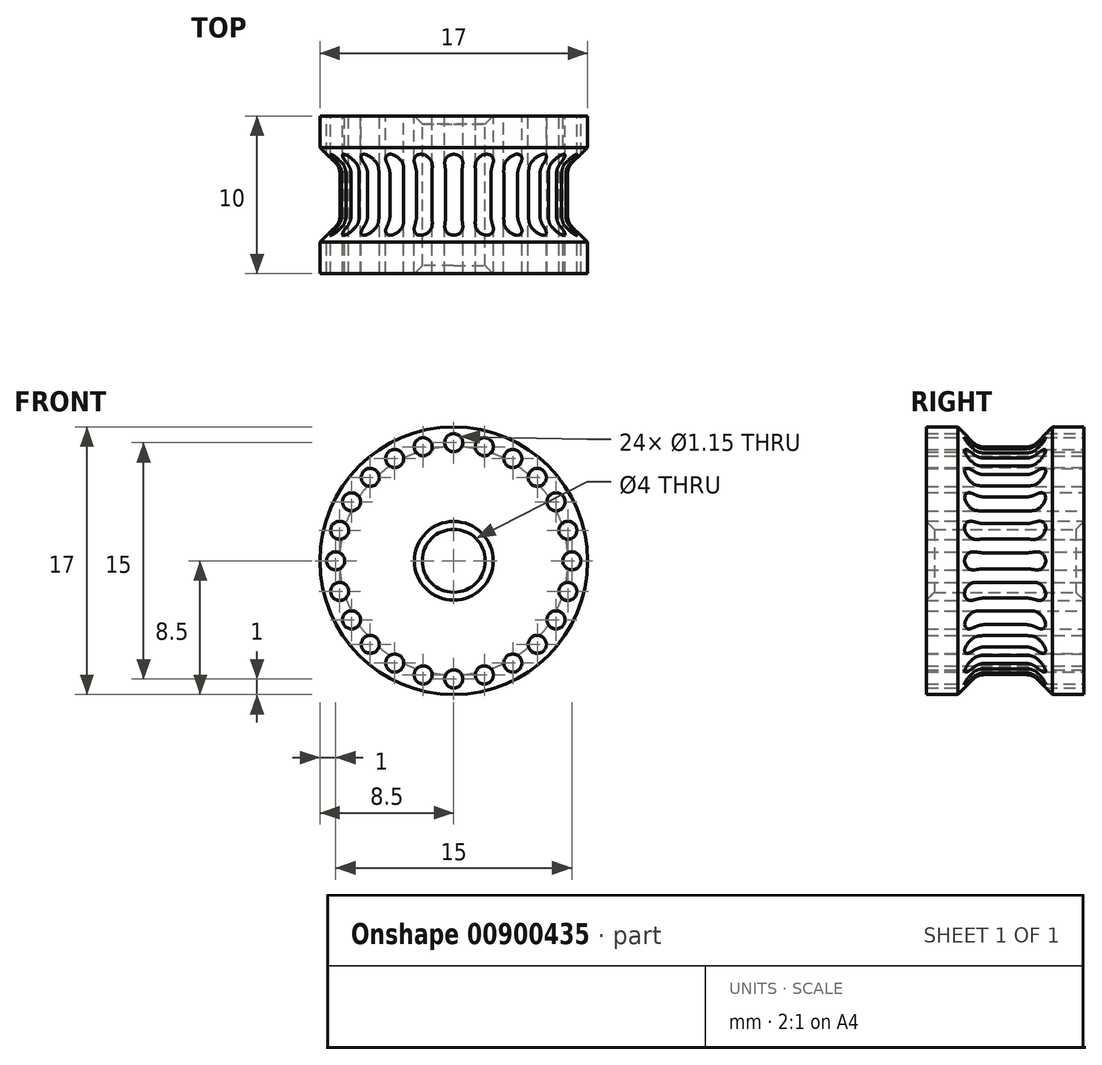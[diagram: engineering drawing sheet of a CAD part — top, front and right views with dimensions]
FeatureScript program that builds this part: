
annotation { "Feature Type Name" : "Feature", "Feature Type Description" : "" }
export const myFeature = defineFeature(function(context is Context, id is Id, definition is map)
    precondition{}
    {
        {
            var Q0;
            Q0=qCreatedBy(makeId("Right.planeOp"),FACE);
            var sketch = newSketch(context, id + "F0", { "sketchPlane" : qUnion([Q0])});
            skLineSegment(sketch, "E0", {"start": v(0, 2) * mm, "end": v(0, 8.5) * mm});
            skLineSegment(sketch, "E1", {"start": v(0, 8.5) * mm, "end": v(-2, 8.5) * mm});
            skLineSegment(sketch, "E2", {"start": v(-2, 8.5) * mm, "end": v(-2.96, 7.54) * mm});
            skLineSegment(sketch, "E3", {"start": v(-3.66, 7.25) * mm, "end": v(-6.34, 7.25) * mm});
            skLineSegment(sketch, "E4", {"start": v(-7.04, 7.54) * mm, "end": v(-8, 8.5) * mm});
            skLineSegment(sketch, "E5", {"start": v(-8, 8.5) * mm, "end": v(-10, 8.5) * mm});
            skLineSegment(sketch, "E6", {"start": v(-10, 8.5) * mm, "end": v(-10, 2) * mm});
            skLineSegment(sketch, "E7", {"start": v(-10, 2) * mm, "end": v(0, 2) * mm});
            skLineSegment(sketch, "E8", {"start": v(-10, 7.5) * mm, "end": v(0, 7.5) * mm, "construction": true});
            skLineSegment(sketch, "E9", {"start": v(-7, 8.5) * mm, "end": v(-7, 7.5) * mm, "construction": true});
            skLineSegment(sketch, "E10", {"start": v(-3, 8.5) * mm, "end": v(-3, 7.5) * mm, "construction": true});
            skLineSegment(sketch, "E11", {"start": v(0, 0) * mm, "end": v(-10, 0) * mm, "construction": true});
            skPoint(sketch, "E12.visualSharp", {"position": v(-6.75, 7.25) * mm});
            skArc(sketch, "E12.filletArc", {"start": v(-7.04, 7.54) * mm, "mid": v(-6.72, 7.33) * mm, "end": v(-6.34, 7.25) * mm});
            skPoint(sketch, "E13.visualSharp", {"position": v(-3.25, 7.25) * mm});
            skArc(sketch, "E13.filletArc", {"start": v(-3.66, 7.25) * mm, "mid": v(-3.28, 7.33) * mm, "end": v(-2.96, 7.54) * mm});
            skSolve(sketch);
        }
        {
            var Q0;
            Q0=makeQuery(id+"F0.imprint","IMPRINT",FACE,{"disambiguationData":[TD([[makeQuery(id+"F0.imprint","IMPRINT",EDGE,{"derivedFrom":sQuery(id+"F0.wireOp",EDGE,"E0")}),1.0]])]});
            var Q1;
            Q1=sQuery(id+"F0.wireOp",EDGE,"E11");
            revolve(context, id + "F1", {"surfaceOperationType" : NewSurfaceOperationType.NEW, "entities" : qUnion([Q0]), "axis" : qUnion([Q1]), "revolveType" : RevolveType.FULL});
        }
        {
            var Q0;
            Q0=qCreatedBy(makeId("Front.planeOp"),FACE);
            var sketch = newSketch(context, id + "F2", { "sketchPlane" : qUnion([Q0])});
            skCircle(sketch, "E14", {"center": v(0, 7.5) * mm, "radius": 0.57 * mm});
            skCircle(sketch, "E15.1.0", {"center": v(-1.94, 7.24) * mm, "radius": 0.57 * mm});
            skCircle(sketch, "E15.2.0", {"center": v(-3.75, 6.5) * mm, "radius": 0.57 * mm});
            skPoint(sketch, "E15.center", {"position": v(0, 0) * mm});
            skCircle(sketch, "E16.1.3.0", {"center": v(-5.3, 5.3) * mm, "radius": 0.57 * mm});
            skCircle(sketch, "E16.1.4.0", {"center": v(-6.5, 3.75) * mm, "radius": 0.57 * mm});
            skCircle(sketch, "E16.1.5.0", {"center": v(-7.24, 1.94) * mm, "radius": 0.57 * mm});
            skCircle(sketch, "E16.1.6.0", {"center": v(-7.5, 0) * mm, "radius": 0.57 * mm});
            skCircle(sketch, "E16.1.7.0", {"center": v(-7.24, -1.94) * mm, "radius": 0.57 * mm});
            skCircle(sketch, "E16.1.8.0", {"center": v(-6.5, -3.75) * mm, "radius": 0.57 * mm});
            skCircle(sketch, "E16.1.9.0", {"center": v(-5.3, -5.3) * mm, "radius": 0.57 * mm});
            skCircle(sketch, "E16.1.10.0", {"center": v(-3.75, -6.5) * mm, "radius": 0.57 * mm});
            skCircle(sketch, "E16.1.11.0", {"center": v(-1.94, -7.24) * mm, "radius": 0.57 * mm});
            skCircle(sketch, "E17.1.12.0", {"center": v(0, -7.5) * mm, "radius": 0.57 * mm});
            skCircle(sketch, "E17.1.13.0", {"center": v(1.94, -7.24) * mm, "radius": 0.57 * mm});
            skCircle(sketch, "E17.1.14.0", {"center": v(3.75, -6.5) * mm, "radius": 0.57 * mm});
            skCircle(sketch, "E17.1.15.0", {"center": v(5.3, -5.3) * mm, "radius": 0.57 * mm});
            skCircle(sketch, "E17.1.16.0", {"center": v(6.5, -3.75) * mm, "radius": 0.57 * mm});
            skCircle(sketch, "E17.1.17.0", {"center": v(7.24, -1.94) * mm, "radius": 0.57 * mm});
            skCircle(sketch, "E17.1.18.0", {"center": v(7.5, 0) * mm, "radius": 0.57 * mm});
            skCircle(sketch, "E17.1.19.0", {"center": v(7.24, 1.94) * mm, "radius": 0.57 * mm});
            skCircle(sketch, "E17.1.20.0", {"center": v(6.5, 3.75) * mm, "radius": 0.57 * mm});
            skCircle(sketch, "E17.1.21.0", {"center": v(5.3, 5.3) * mm, "radius": 0.57 * mm});
            skCircle(sketch, "E17.1.22.0", {"center": v(3.75, 6.5) * mm, "radius": 0.57 * mm});
            skCircle(sketch, "E17.1.23.0", {"center": v(1.94, 7.24) * mm, "radius": 0.57 * mm});
            skSolve(sketch);
        }
        {
            var Q0;
            Q0=makeQuery(id+"F2.imprint","IMPRINT",FACE,{"disambiguationData":[TD([[makeQuery(id+"F2.imprint","IMPRINT",EDGE,{"derivedFrom":sQuery(id+"F2.wireOp",EDGE,"E16.1.11.0")}),1.0]])]});
            var Q1;
            Q1=makeQuery(id+"F2.imprint","IMPRINT",FACE,{"disambiguationData":[TD([[makeQuery(id+"F2.imprint","IMPRINT",EDGE,{"derivedFrom":sQuery(id+"F2.wireOp",EDGE,"E17.1.14.0")}),1.0]])]});
            var Q2;
            Q2=makeQuery(id+"F2.imprint","IMPRINT",FACE,{"disambiguationData":[TD([[makeQuery(id+"F2.imprint","IMPRINT",EDGE,{"derivedFrom":sQuery(id+"F2.wireOp",EDGE,"E16.1.8.0")}),1.0]])]});
            var Q3;
            Q3=makeQuery(id+"F2.imprint","IMPRINT",FACE,{"disambiguationData":[TD([[makeQuery(id+"F2.imprint","IMPRINT",EDGE,{"derivedFrom":sQuery(id+"F2.wireOp",EDGE,"E15.2.0")}),1.0]])]});
            var Q4;
            Q4=makeQuery(id+"F2.imprint","IMPRINT",FACE,{"disambiguationData":[TD([[makeQuery(id+"F2.imprint","IMPRINT",EDGE,{"derivedFrom":sQuery(id+"F2.wireOp",EDGE,"E16.1.7.0")}),1.0]])]});
            var Q5;
            Q5=makeQuery(id+"F2.imprint","IMPRINT",FACE,{"disambiguationData":[TD([[makeQuery(id+"F2.imprint","IMPRINT",EDGE,{"derivedFrom":sQuery(id+"F2.wireOp",EDGE,"E16.1.4.0")}),1.0]])]});
            var Q6;
            Q6=makeQuery(id+"F2.imprint","IMPRINT",FACE,{"disambiguationData":[TD([[makeQuery(id+"F2.imprint","IMPRINT",EDGE,{"derivedFrom":sQuery(id+"F2.wireOp",EDGE,"E17.1.23.0")}),1.0]])]});
            var Q7;
            Q7=makeQuery(id+"F2.imprint","IMPRINT",FACE,{"disambiguationData":[TD([[makeQuery(id+"F2.imprint","IMPRINT",EDGE,{"derivedFrom":sQuery(id+"F2.wireOp",EDGE,"E17.1.15.0")}),1.0]])]});
            var Q8;
            Q8=makeQuery(id+"F2.imprint","IMPRINT",FACE,{"disambiguationData":[TD([[makeQuery(id+"F2.imprint","IMPRINT",EDGE,{"derivedFrom":sQuery(id+"F2.wireOp",EDGE,"E17.1.20.0")}),1.0]])]});
            var Q9;
            Q9=makeQuery(id+"F2.imprint","IMPRINT",FACE,{"disambiguationData":[TD([[makeQuery(id+"F2.imprint","IMPRINT",EDGE,{"derivedFrom":sQuery(id+"F2.wireOp",EDGE,"E15.1.0")}),1.0]])]});
            var Q10;
            Q10=makeQuery(id+"F2.imprint","IMPRINT",FACE,{"disambiguationData":[TD([[makeQuery(id+"F2.imprint","IMPRINT",EDGE,{"derivedFrom":sQuery(id+"F2.wireOp",EDGE,"E17.1.17.0")}),1.0]])]});
            var Q11;
            Q11=makeQuery(id+"F2.imprint","IMPRINT",FACE,{"disambiguationData":[TD([[makeQuery(id+"F2.imprint","IMPRINT",EDGE,{"derivedFrom":sQuery(id+"F2.wireOp",EDGE,"E16.1.6.0")}),1.0]])]});
            var Q12;
            Q12=makeQuery(id+"F2.imprint","IMPRINT",FACE,{"disambiguationData":[TD([[makeQuery(id+"F2.imprint","IMPRINT",EDGE,{"derivedFrom":sQuery(id+"F2.wireOp",EDGE,"E16.1.3.0")}),1.0]])]});
            var Q13;
            Q13=makeQuery(id+"F2.imprint","IMPRINT",FACE,{"disambiguationData":[TD([[makeQuery(id+"F2.imprint","IMPRINT",EDGE,{"derivedFrom":sQuery(id+"F2.wireOp",EDGE,"E17.1.22.0")}),1.0]])]});
            var Q14;
            Q14=makeQuery(id+"F2.imprint","IMPRINT",FACE,{"disambiguationData":[TD([[makeQuery(id+"F2.imprint","IMPRINT",EDGE,{"derivedFrom":sQuery(id+"F2.wireOp",EDGE,"E16.1.10.0")}),1.0]])]});
            var Q15;
            Q15=makeQuery(id+"F2.imprint","IMPRINT",FACE,{"disambiguationData":[TD([[makeQuery(id+"F2.imprint","IMPRINT",EDGE,{"derivedFrom":sQuery(id+"F2.wireOp",EDGE,"E17.1.21.0")}),1.0]])]});
            var Q16;
            Q16=makeQuery(id+"F2.imprint","IMPRINT",FACE,{"disambiguationData":[TD([[makeQuery(id+"F2.imprint","IMPRINT",EDGE,{"derivedFrom":sQuery(id+"F2.wireOp",EDGE,"E17.1.13.0")}),1.0]])]});
            var Q17;
            Q17=makeQuery(id+"F2.imprint","IMPRINT",FACE,{"disambiguationData":[TD([[makeQuery(id+"F2.imprint","IMPRINT",EDGE,{"derivedFrom":sQuery(id+"F2.wireOp",EDGE,"E17.1.19.0")}),1.0]])]});
            var Q18;
            Q18=makeQuery(id+"F2.imprint","IMPRINT",FACE,{"disambiguationData":[TD([[makeQuery(id+"F2.imprint","IMPRINT",EDGE,{"derivedFrom":sQuery(id+"F2.wireOp",EDGE,"E16.1.5.0")}),1.0]])]});
            var Q19;
            Q19=makeQuery(id+"F2.imprint","IMPRINT",FACE,{"disambiguationData":[TD([[makeQuery(id+"F2.imprint","IMPRINT",EDGE,{"derivedFrom":sQuery(id+"F2.wireOp",EDGE,"E17.1.12.0")}),1.0]])]});
            var Q20;
            Q20=makeQuery(id+"F2.imprint","IMPRINT",FACE,{"disambiguationData":[TD([[makeQuery(id+"F2.imprint","IMPRINT",EDGE,{"derivedFrom":sQuery(id+"F2.wireOp",EDGE,"E17.1.16.0")}),1.0]])]});
            var Q21;
            Q21=makeQuery(id+"F2.imprint","IMPRINT",FACE,{"disambiguationData":[TD([[makeQuery(id+"F2.imprint","IMPRINT",EDGE,{"derivedFrom":sQuery(id+"F2.wireOp",EDGE,"E14")}),1.0]])]});
            var Q22;
            Q22=makeQuery(id+"F2.imprint","IMPRINT",FACE,{"disambiguationData":[TD([[makeQuery(id+"F2.imprint","IMPRINT",EDGE,{"derivedFrom":sQuery(id+"F2.wireOp",EDGE,"E17.1.18.0")}),1.0]])]});
            var Q23;
            Q23=makeQuery(id+"F2.imprint","IMPRINT",FACE,{"disambiguationData":[TD([[makeQuery(id+"F2.imprint","IMPRINT",EDGE,{"derivedFrom":sQuery(id+"F2.wireOp",EDGE,"E16.1.9.0")}),1.0]])]});
            extrude(context, id + "F3", {"entities" : qUnion([Q0, Q1, Q2, Q3, Q4, Q5, Q6, Q7, Q8, Q9, Q10, Q11, Q12, Q13, Q14, Q15, Q16, Q17, Q18, Q19, Q20, Q21, Q22, Q23]), "operationType" : NewBodyOperationType.REMOVE, "depth" : 20 * mm, "offsetDistance" : 25 * mm});
        }
        {
            var Q0;
            Q0=makeQuery(id+"F1.opRevolve","SWEPT_FACE",FACE,{"disambiguationData":[OSD([sQuery(id+"F0.wireOp",EDGE,"E7")])]});
            chamfer(context, id + "F4", {"entities" : qUnion([Q0]), "width" : 0.5 * mm, "tangentPropagation" : true});
        }
    });
